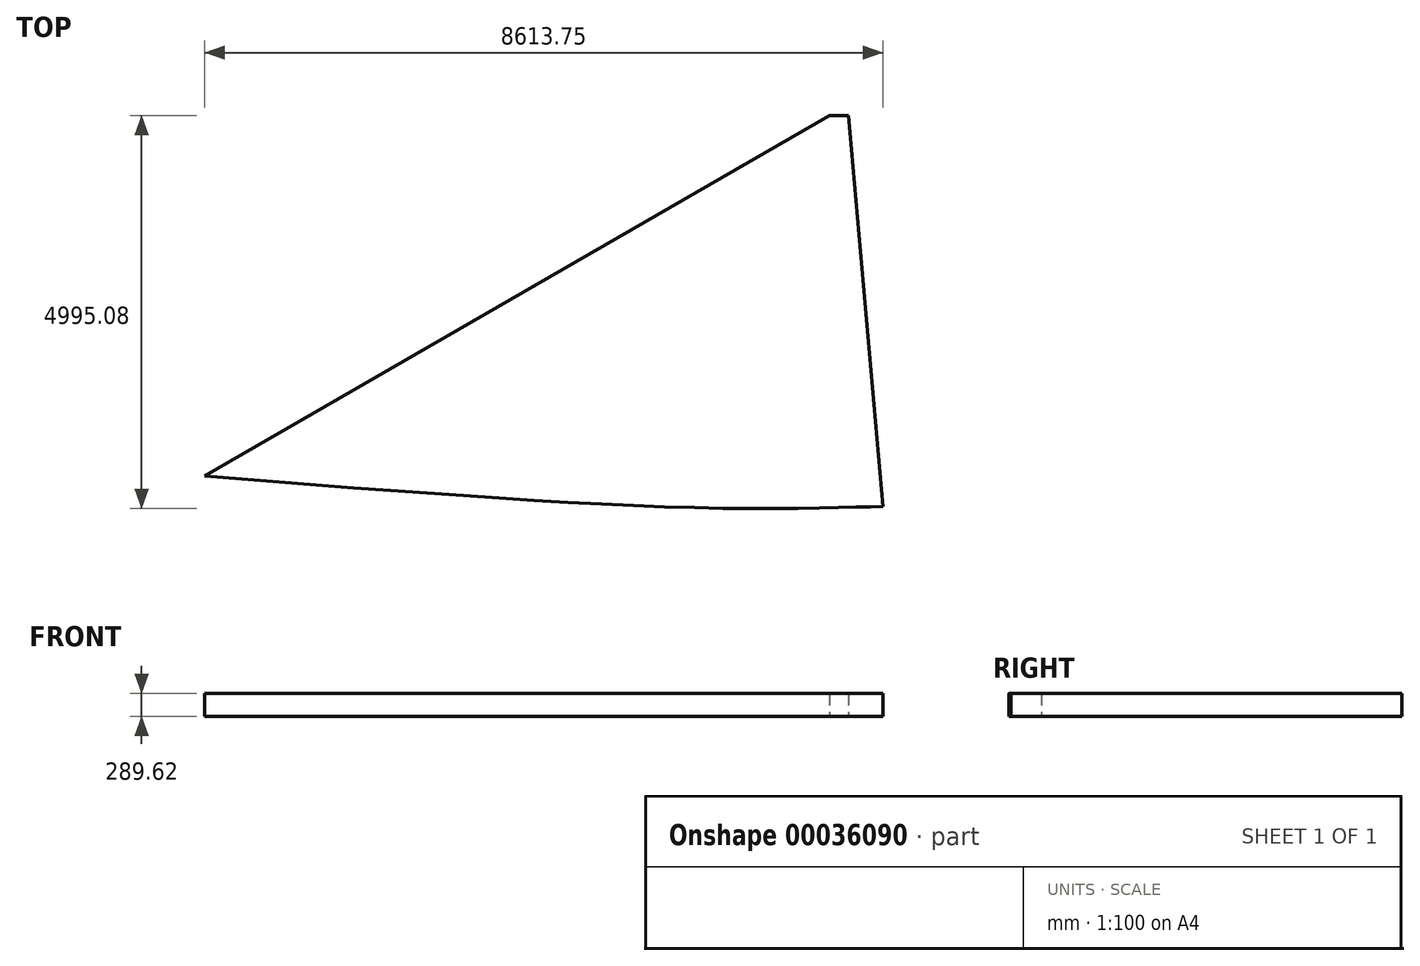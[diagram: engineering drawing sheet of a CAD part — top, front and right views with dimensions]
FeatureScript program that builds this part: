
annotation { "Feature Type Name" : "Feature", "Feature Type Description" : "" }
export const myFeature = defineFeature(function(context is Context, id is Id, definition is map)
    precondition{}
    {
        {
            var Q0;
            Q0=qCreatedBy(makeId("Top.planeOp"),FACE);
            var sketch = newSketch(context, id + "F0", { "sketchPlane" : qUnion([Q0])});
            skLineSegment(sketch, "E0", {"start": v(0, 0) * mm, "end": v(10107.64, 5835.65) * mm});
            skLineSegment(sketch, "E1", {"start": v(10861.04, 0) * mm, "end": v(0, 0) * mm});
            skLineSegment(sketch, "E2", {"start": v(10107.64, 5835.65) * mm, "end": v(10350.49, 5835.65) * mm});
            skLineSegment(sketch, "E3", {"start": v(10861.04, 0) * mm, "end": v(10350.49, 5835.65) * mm});
            skSolve(sketch);
        }
        {
            var Q0;
            Q0=makeQuery(id+"F0.imprint","IMPRINT",FACE,{"disambiguationData":[TD([[makeQuery(id+"F0.imprint","IMPRINT",EDGE,{"derivedFrom":sQuery(id+"F0.wireOp",EDGE,"E0")}),-1.0]])]});
            var sketch = newSketch(context, id + "F1", { "sketchPlane" : qUnion([Q0])});
            skLineSegment(sketch, "E4", {"start": v(2171.45, 2095.8) * mm, "end": v(2171.45, -777.95) * mm, "construction": true});
            skLineSegment(sketch, "E5", {"start": v(10861.04, 1272.68) * mm, "end": v(10861.04, -670.62) * mm, "construction": true});
            skFitSpline(sketch, "E6", {"points": [v(2171.45, 1253.68) * mm, v(8810.75, 843.79) * mm, v(10861.04, 867.4) * mm], "startDerivative": vector(11078.91, -881.61) * mm, "endDerivative": vector(2816.68, 0) * mm});
            skLineSegment(sketch, "E7", {"start": v(2171.45, 1253.68) * mm, "end": v(10107.64, 5835.65) * mm});
            skLineSegment(sketch, "E8", {"start": v(10107.64, 5835.65) * mm, "end": v(10350.49, 5835.65) * mm});
            skLineSegment(sketch, "E9", {"start": v(10350.49, 5835.65) * mm, "end": v(10785.2, 866.89) * mm});
            skSolve(sketch);
        }
        {
            var Q0;
            Q0 = qSketchRegion(id + "F1", true);
            extrude(context, id + "F2", {"entities" : qUnion([Q0]), "depth" : 289.62 * mm});
        }
    });
